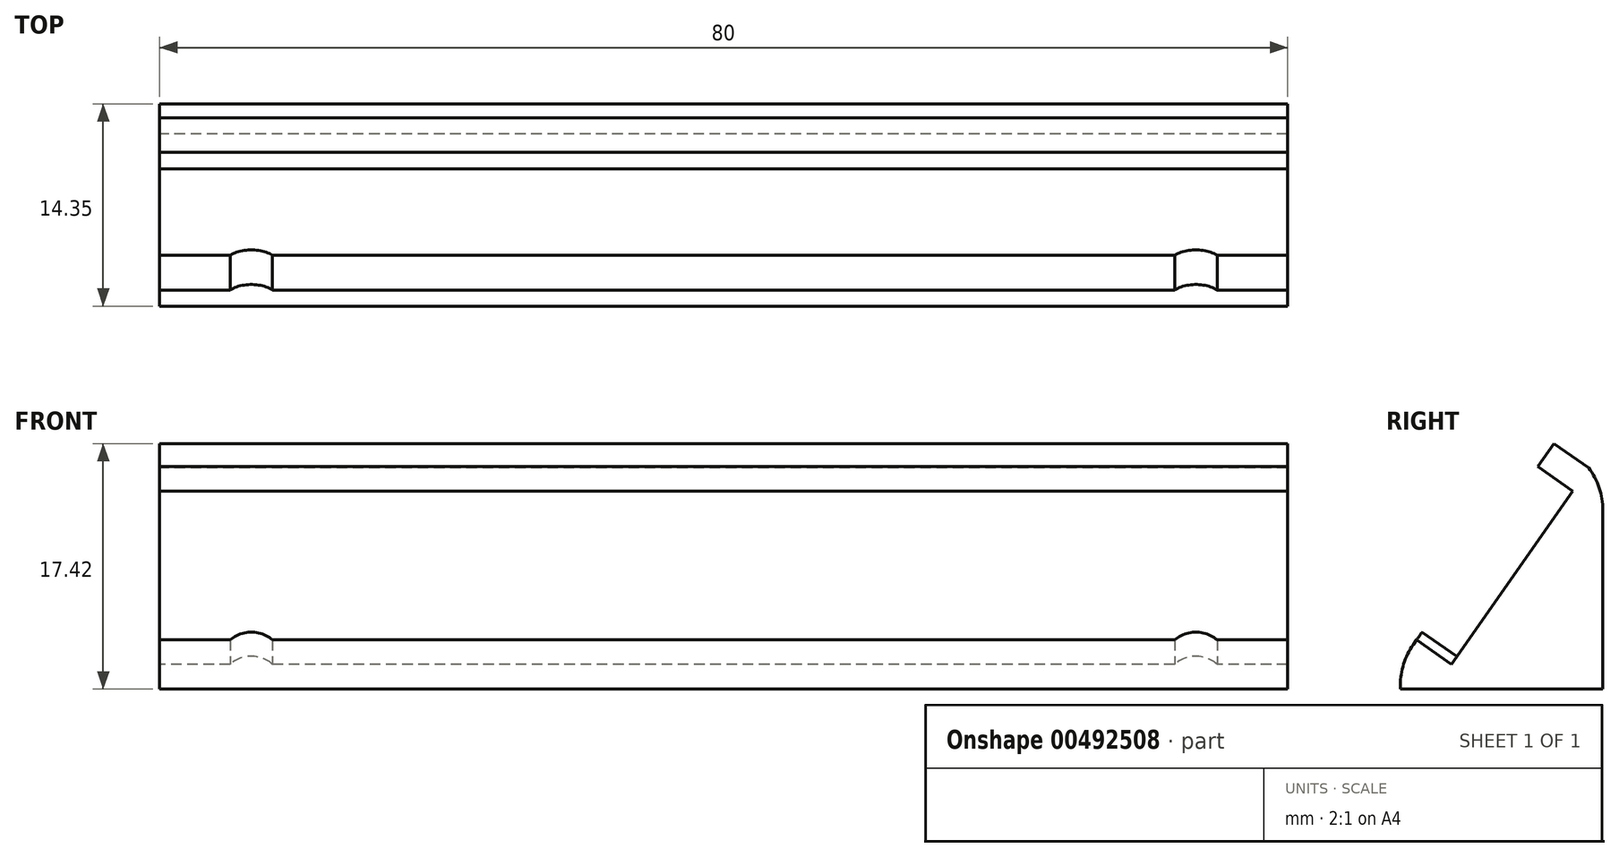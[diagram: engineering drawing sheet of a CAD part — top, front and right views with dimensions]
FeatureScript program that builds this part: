
annotation { "Feature Type Name" : "Feature", "Feature Type Description" : "" }
export const myFeature = defineFeature(function(context is Context, id is Id, definition is map)
    precondition{}
    {
        {
            var Q0;
            Q0=qCreatedBy(makeId("Right.planeOp"),FACE);
            var sketch = newSketch(context, id + "F0", { "sketchPlane" : qUnion([Q0])});
            skLineSegment(sketch, "E0", {"start": v(0, 0) * mm, "end": v(11, 15.7) * mm});
            skLineSegment(sketch, "E1", {"start": v(11, 15.7) * mm, "end": v(12, 15.7) * mm});
            skLineSegment(sketch, "E2", {"start": v(12, 15.7) * mm, "end": v(12, 0) * mm});
            skLineSegment(sketch, "E3", {"start": v(12, 0) * mm, "end": v(0, 0) * mm});
            skLineSegment(sketch, "E4", {"start": v(11, 15.7) * mm, "end": v(8.54, 17.42) * mm});
            skLineSegment(sketch, "E5", {"start": v(8.54, 17.42) * mm, "end": v(7.39, 15.78) * mm});
            skLineSegment(sketch, "E6", {"start": v(7.39, 15.78) * mm, "end": v(9.85, 14.06) * mm});
            skLineSegment(sketch, "E7", {"start": v(1.24, 1.77) * mm, "end": v(-1.21, 3.5) * mm});
            skLineSegment(sketch, "E8", {"start": v(-1.21, 3.5) * mm, "end": v(-2.36, 1.86) * mm});
            skLineSegment(sketch, "E9", {"start": v(-2.36, 1.86) * mm, "end": v(0.1, 0.14) * mm});
            skLineSegment(sketch, "E10", {"start": v(-2.36, 1.86) * mm, "end": v(-2.36, 0) * mm});
            skLineSegment(sketch, "E11", {"start": v(-2.36, 0) * mm, "end": v(0, 0) * mm});
            skSolve(sketch);
        }
        {
            var Q0;
            {var subQ0=sQuery(id+"F0.wireOp",EDGE,"E1");Q0=makeQuery(id+"F0.imprint","IMPRINT",FACE,{"disambiguationData":[TD([[makeQuery(id+"F0.imprint","IMPRINT",EDGE,{"derivedFrom":subQ0}),-1.0]])]});}
            var Q1;
            {var subQ0=sQuery(id+"F0.wireOp",EDGE,"E4");Q1=makeQuery(id+"F0.imprint","IMPRINT",FACE,{"disambiguationData":[TD([[makeQuery(id+"F0.imprint","IMPRINT",EDGE,{"derivedFrom":subQ0}),1.0]])]});}
            var Q2;
            {var subQ0=sQuery(id+"F0.wireOp",EDGE,"E7");Q2=makeQuery(id+"F0.imprint","IMPRINT",FACE,{"disambiguationData":[TD([[makeQuery(id+"F0.imprint","IMPRINT",EDGE,{"derivedFrom":subQ0}),1.0]])]});}
            var Q3;
            {var subQ2=sQuery(id+"F0.wireOp",EDGE,"E9");Q3=makeQuery(id+"F0.imprint","IMPRINT",FACE,{"disambiguationData":[TD([[makeQuery(id+"F0.imprint","IMPRINT",EDGE,{"derivedFrom":subQ2}),-1.0]])]});}
            extrude(context, id + "F1", {"entities" : qUnion([Q0, Q1, Q2, Q3]), "endBound" : BoundingType.SYMMETRIC, "depth" : 80 * mm});
        }
        {
            var Q0;
            Q0=makeQuery(id+"F1.opExtrude","SWEPT_EDGE",EDGE,{"disambiguationData":[OSD([sQuery(id+"F0.wireOp",EDGE,"E8"),sQuery(id+"F0.wireOp",EDGE,"E9"),sQuery(id+"F0.wireOp",EDGE,"E10")])]});
            fillet(context, id + "F2", {"entities" : qUnion([Q0]), "radius" : 5 * mm, "tangentPropagation" : true, "allowEdgeOverflow" : false});
        }
        {
            var Q0;
            Q0=makeQuery(id+"F1.opExtrude","SWEPT_EDGE",EDGE,{"disambiguationData":[OSD([sQuery(id+"F0.wireOp",EDGE,"E1"),sQuery(id+"F0.wireOp",EDGE,"E2")])]});
            fillet(context, id + "F3", {"entities" : qUnion([Q0]), "radius" : 5 * mm, "tangentPropagation" : true, "allowEdgeOverflow" : false});
        }
        {
            var Q0;
            Q0=makeQuery(id+"F1.opExtrude","SWEPT_FACE",FACE,{"disambiguationData":[OSD([sQuery(id+"F0.wireOp",EDGE,"E0")])]});
            var sketch = newSketch(context, id + "F4", { "sketchPlane" : qUnion([Q0])});
            skArc(sketch, "E12", {"start": v(-32, 2.17) * mm, "mid": v(-33.5, 2.84) * mm, "end": v(-35, 2.17) * mm});
            skArc(sketch, "E13", {"start": v(35, 2.17) * mm, "mid": v(33.5, 2.84) * mm, "end": v(32, 2.17) * mm});
            skSolve(sketch);
        }
        {
            var Q0;
            {var subQ0=sQuery(id+"F4.wireOp",EDGE,"E12");Q0=makeQuery(id+"F4.imprint","IMPRINT",FACE,{"disambiguationData":[TD([[makeQuery(id+"F4.imprint","IMPRINT",EDGE,{"derivedFrom":subQ0}),1.0]])]});}
            var Q1;
            {var subQ0=sQuery(id+"F4.wireOp",EDGE,"E13");Q1=makeQuery(id+"F4.imprint","IMPRINT",FACE,{"disambiguationData":[TD([[makeQuery(id+"F4.imprint","IMPRINT",EDGE,{"derivedFrom":subQ0}),1.0]])]});}
            extrude(context, id + "F5", {"entities" : qUnion([Q0, Q1]), "operationType" : NewBodyOperationType.ADD, "depth" : 3 * mm});
        }
    });
